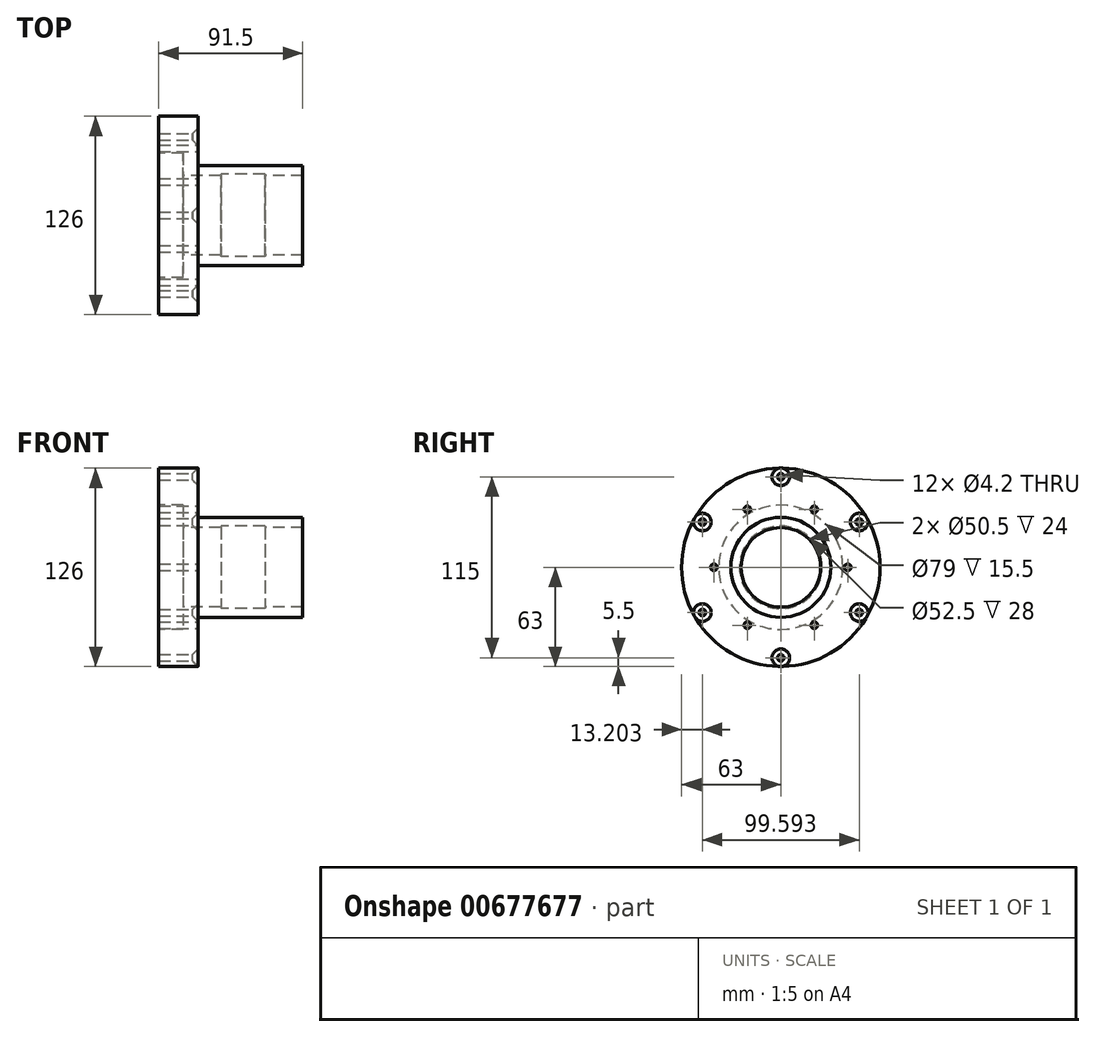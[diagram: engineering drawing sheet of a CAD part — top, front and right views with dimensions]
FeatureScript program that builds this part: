
annotation { "Feature Type Name" : "Feature", "Feature Type Description" : "" }
export const myFeature = defineFeature(function(context is Context, id is Id, definition is map)
    precondition{}
    {
        {
            var Q0;
            Q0=qCreatedBy(makeId("Front.planeOp"),FACE);
            var sketch = newSketch(context, id + "F0", { "sketchPlane" : qUnion([Q0])});
            skLineSegment(sketch, "E0", {"start": v(-62.85, 0) * mm, "end": v(77.66, 0) * mm, "construction": true});
            skLineSegment(sketch, "E1", {"start": v(52, 25.25) * mm, "end": v(28, 25.25) * mm});
            skLineSegment(sketch, "E2", {"start": v(-24, 25.25) * mm, "end": v(-24, 39.5) * mm});
            skLineSegment(sketch, "E3", {"start": v(-24, 39.5) * mm, "end": v(-39.5, 39.5) * mm});
            skLineSegment(sketch, "E4", {"start": v(-39.5, 39.5) * mm, "end": v(-39.5, 63) * mm});
            skLineSegment(sketch, "E5", {"start": v(-39.5, 63) * mm, "end": v(-14.5, 63) * mm});
            skLineSegment(sketch, "E6", {"start": v(-14.5, 63) * mm, "end": v(-14.5, 31.75) * mm});
            skLineSegment(sketch, "E7", {"start": v(-14.5, 31.75) * mm, "end": v(52, 31.75) * mm});
            skLineSegment(sketch, "E8", {"start": v(52, 31.75) * mm, "end": v(52, 25.25) * mm});
            skLineSegment(sketch, "E9", {"start": v(28, 25.25) * mm, "end": v(28, 26.25) * mm});
            skLineSegment(sketch, "E10", {"start": v(28, 26.25) * mm, "end": v(0, 26.25) * mm});
            skLineSegment(sketch, "E11", {"start": v(0, 26.25) * mm, "end": v(0, 25.25) * mm});
            skLineSegment(sketch, "E12.trimOffspring", {"start": v(0, 25.25) * mm, "end": v(-24, 25.25) * mm});
            skSolve(sketch);
        }
        {
            var Q0;
            Q0=makeQuery(id+"F0.imprint","IMPRINT",FACE,{"disambiguationData":[TD([[makeQuery(id+"F0.imprint","IMPRINT",EDGE,{"derivedFrom":sQuery(id+"F0.wireOp",EDGE,"E1")}),-1.0]])]});
            var Q1;
            Q1=sQuery(id+"F0.wireOp",EDGE,"E0");
            revolve(context, id + "F1", {"entities" : qUnion([Q0]), "axis" : qUnion([Q1]), "revolveType" : RevolveType.FULL});
        }
        {
            var Q0;
            Q0=makeQuery(id+"F1.opRevolve","SWEPT_FACE",FACE,{"disambiguationData":[OSD([sQuery(id+"F0.wireOp",EDGE,"E6")])]});
            var sketch = newSketch(context, id + "F2", { "sketchPlane" : qUnion([Q0])});
            skCircle(sketch, "E13", {"center": v(0, 0) * mm, "radius": 57.5 * mm, "construction": true});
            skPoint(sketch, "E14", {"position": v(0, 57.5) * mm});
            skPoint(sketch, "E15", {"position": v(0, -57.5) * mm});
            skLineSegment(sketch, "E16", {"start": v(-75.79, 0) * mm, "end": v(105.9, 0) * mm, "construction": true});
            skLineSegment(sketch, "E17", {"start": v(-72.63, 41.93) * mm, "end": v(85.02, -49.09) * mm, "construction": true});
            skLineSegment(sketch, "E18", {"start": v(66.36, 38.31) * mm, "end": v(-72.7, -41.97) * mm, "construction": true});
            skLineSegment(sketch, "E19", {"start": v(0, 71.75) * mm, "end": v(0, -73.41) * mm, "construction": true});
            skPoint(sketch, "E20", {"position": v(-49.8, 28.75) * mm});
            skPoint(sketch, "E21", {"position": v(-49.8, -28.75) * mm});
            skPoint(sketch, "E22", {"position": v(49.8, -28.75) * mm});
            skPoint(sketch, "E23", {"position": v(49.8, 28.75) * mm});
            skSolve(sketch);
        }
        {
            var Q0;
            Q0=sQuery(id+"F2.wireOp",VERTEX,"E14");
            var Q1;
            Q1=sQuery(id+"F2.wireOp",VERTEX,"E23");
            var Q2;
            Q2=sQuery(id+"F2.wireOp",VERTEX,"E22");
            var Q3;
            Q3=sQuery(id+"F2.wireOp",VERTEX,"E21");
            var Q4;
            Q4=sQuery(id+"F2.wireOp",VERTEX,"E15");
            var Q5;
            Q5=sQuery(id+"F2.wireOp",VERTEX,"E20");
            var Q6;
            Q6=makeQuery(id+"F1.opRevolve","SWEPT_BODY",BODY,{"disambiguationData":[OSD([sQuery(id+"F0.wireOp",EDGE,"E1"),sQuery(id+"F0.wireOp",EDGE,"E2"),sQuery(id+"F0.wireOp",EDGE,"E3"),sQuery(id+"F0.wireOp",EDGE,"E4"),sQuery(id+"F0.wireOp",EDGE,"E5"),sQuery(id+"F0.wireOp",EDGE,"E6"),sQuery(id+"F0.wireOp",EDGE,"E7"),sQuery(id+"F0.wireOp",EDGE,"E8"),sQuery(id+"F0.wireOp",EDGE,"E9"),sQuery(id+"F0.wireOp",EDGE,"E10"),sQuery(id+"F0.wireOp",EDGE,"E11"),sQuery(id+"F0.wireOp",EDGE,"E12.trimOffspring")])]});
            hole(context, id + "F3", {"style" : HoleStyle.C_SINK, "endStyle" : HoleEndStyle.THROUGH, "standardTappedOrClearance" : lookupTablePath({ "standard" : "ISO", "engagement" : "75%", "pitch" : "0.8 mm", "size" : "M5", "type" : "Tapped" }), "standardBlindInLast" : lookupTablePath({ "standard" : "ISO", "engagement" : "75%", "pitch" : "0.8 mm", "size" : "M5", "type" : "Tapped" }), "holeDiameter" : 4.2 * mm, "cSinkDiameter" : 11.2 * mm, "cSinkAngle" : 90 * degree, "majorDiameter" : 5 * mm, "showTappedDepth" : true, "isTappedThrough" : true, "tappedDepth" : 16.25 * mm, "tapClearance" : 3, "locations" : qUnion([Q0, Q1, Q2, Q3, Q4, Q5]), "scope" : qUnion([Q6])});
        }
        {
            var Q0;
            Q0=makeQuery(id+"F1.opRevolve","SWEPT_FACE",FACE,{"disambiguationData":[OSD([sQuery(id+"F0.wireOp",EDGE,"E6")])]});
            var sketch = newSketch(context, id + "F4", { "sketchPlane" : qUnion([Q0])});
            skCircle(sketch, "E24", {"center": v(0, 0) * mm, "radius": 42.5 * mm, "construction": true});
            skLineSegment(sketch, "E25", {"start": v(-71.75, 0) * mm, "end": v(81.48, 0) * mm, "construction": true});
            skPoint(sketch, "E25.endSnap0", {"position": v(-63, 0) * mm});
            skLineSegment(sketch, "E26", {"start": v(-36.98, 64.06) * mm, "end": v(44.45, -76.98) * mm, "construction": true});
            skLineSegment(sketch, "E27", {"start": v(-36.31, -62.9) * mm, "end": v(38, 65.82) * mm, "construction": true});
            skPoint(sketch, "E28", {"position": v(-21.25, 36.8) * mm});
            skPoint(sketch, "E29", {"position": v(21.25, 36.8) * mm});
            skPoint(sketch, "E30", {"position": v(42.5, 0) * mm});
            skPoint(sketch, "E31", {"position": v(21.25, -36.8) * mm});
            skPoint(sketch, "E32", {"position": v(-21.25, -36.8) * mm});
            skPoint(sketch, "E33", {"position": v(-42.5, 0) * mm});
            skSolve(sketch);
        }
        {
            var Q0;
            Q0=sQuery(id+"F4.wireOp",VERTEX,"E28");
            var Q1;
            Q1=sQuery(id+"F4.wireOp",VERTEX,"E29");
            var Q2;
            Q2=sQuery(id+"F4.wireOp",VERTEX,"E30");
            var Q3;
            Q3=sQuery(id+"F4.wireOp",VERTEX,"E31");
            var Q4;
            Q4=sQuery(id+"F4.wireOp",VERTEX,"E32");
            var Q5;
            Q5=sQuery(id+"F4.wireOp",VERTEX,"E33");
            var Q6;
            Q6=makeQuery(id+"F1.opRevolve","SWEPT_BODY",BODY,{"disambiguationData":[OSD([sQuery(id+"F0.wireOp",EDGE,"E1"),sQuery(id+"F0.wireOp",EDGE,"E2"),sQuery(id+"F0.wireOp",EDGE,"E3"),sQuery(id+"F0.wireOp",EDGE,"E4"),sQuery(id+"F0.wireOp",EDGE,"E5"),sQuery(id+"F0.wireOp",EDGE,"E6"),sQuery(id+"F0.wireOp",EDGE,"E7"),sQuery(id+"F0.wireOp",EDGE,"E8"),sQuery(id+"F0.wireOp",EDGE,"E9"),sQuery(id+"F0.wireOp",EDGE,"E10"),sQuery(id+"F0.wireOp",EDGE,"E11"),sQuery(id+"F0.wireOp",EDGE,"E12.trimOffspring")])]});
            hole(context, id + "F5", {"style" : HoleStyle.SIMPLE, "endStyle" : HoleEndStyle.THROUGH, "standardTappedOrClearance" : lookupTablePath({ "standard" : "ISO", "engagement" : "75%", "pitch" : "0.8 mm", "size" : "M5", "type" : "Tapped" }), "standardBlindInLast" : lookupTablePath({ "standard" : "ISO", "engagement" : "75%", "pitch" : "0.8 mm", "size" : "M5", "type" : "Tapped" }), "holeDiameter" : 4.2 * mm, "majorDiameter" : 5 * mm, "showTappedDepth" : true, "isTappedThrough" : true, "tappedDepth" : 16.25 * mm, "tapClearance" : 3, "locations" : qUnion([Q0, Q1, Q2, Q3, Q4, Q5]), "scope" : qUnion([Q6])});
        }
    });
